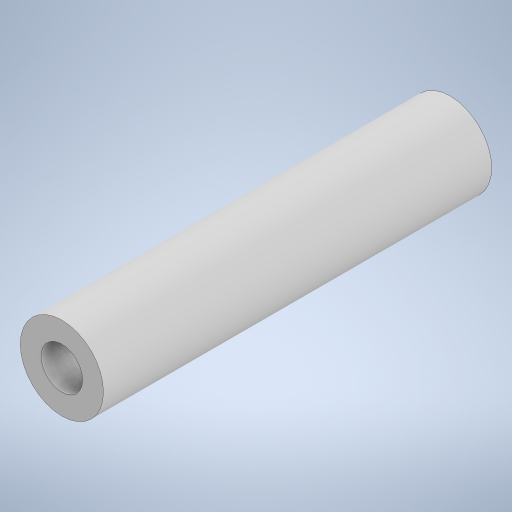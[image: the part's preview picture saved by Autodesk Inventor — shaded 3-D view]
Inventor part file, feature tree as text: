
AUTODESK INVENTOR PART (.ipt)
format: ipt  version: 2024.3 (Build 283343000, 343)  size: 219,136 bytes
history: native  units: mm
features: other x1, extrude x1, sketch x1
ambient origin geometry x8: Origin, YZ Plane, XZ Plane, XY Plane, X Axis, Y Axis, Z Axis, Center Point
bodies: Body1 (feature_tree)
feature tree (3):
  other  "ソリッド1"
  extrude  "押し出し1"  Depth=6.0mm
  sketch  "スケッチ1"
